# Revit family: Neri_Light Hydra_PUHYDL-Dppp
name_source: partatom
category: Apparecchi per illuminazione
revit_build: Autodesk Revit LT 2018 (Build: 20170223_1515(x64)
units: mm (PartAtom-declared; Revit-internal decimal feet)

## family parameters
Basato su piano di lavoro = No
Condiviso = No
Numero OmniClass = 23.35.47.11
Punto di calcolo locali = No
Quota connettore circolare = Usa diametro
Sempre verticale = Sì
Sorgente d'illuminazione = Sì
Taglio con vuoti quando caricato = No
Tipo di parte = Normale

## types (1)
- PNHYDL_NLG04
    Angolo inclinazione = 90.00°
    CRI = >70
    Class IES = Semi Cut-Off
    Connection = Upright installation on head post or bracket - Hole diam.1,10" for attachment to the support
    Control = COD 02= 1-10V + NCL
    Data Sheet = https://www.nerinorthamerica.com
    Design Country = Italy
    EPA = 0.834 ft²
    Estimated Life = 80.000 h (L85 - Ta 25°C)
    Fasteners = Stainless Steel
    File diagramma fotometrico = PUHYDL_NLG04.IES
    Filtro dei colori = 16777215
    Frequency = 50-60 Hz
    Height = 1' - 11 3/4"
    Height of Installation = From 13.0' to 16.5'
    IK = 06
    IP = 43
    Immagine tipo = <Nessuno>
    LOR = 90 %
    Lampada = LED
    Lenght = 1' - 4 1/2"
    Lighting Distribution/Class = Asymmetric - Mixed Areas
    Luminaire Classification Sysytem = BUG: B1 U3 G1
    Luminous Efficacy = 79 Lm/W
    Manufacturer Country = Italy
    Manufacturer Name = Neri SpA
    MasterFormat 2016 Code = 26 56 00
    MasterFormat 2016 Description = Exterior Lighting
    Material Main = Cast Aluminum
    Modello = PUHYDL-D
    NBS_UniClass2015 Code = Ss_70_80_25_70
    NBS_UniClass2015 Description = Roadway Lighting Systems
    OmniClass Code = 23-35 47 11
    OmniClass Description = Lighting Fixtures
    Operative Temperature = -22°F / +104°F
    Optics = NLG04
    Overvoltage Protection = 4kV/4kV (differential / common mode)
    Painting = Standard color: Exterior Frame_matt black (RAL 9005) - Inside Frame_White (RAL 9010)
    Painting Steps = Information about paint steps used in this product in specific technical sheet
    Product Certification = UL Standard 1598 (C, US)
    Product Name = Light Hydra - LED D
    Produttore = Neri SpA
    Screen = Tempered transparent flat glass
    URL = https://www.nerinorthamerica.com
    UniFormat II Code = D5020
    UniFormat II Description = Lighting and Branch Wiring
    Variazione temperatura colore lampada con luminosità attenuata = <Nessuno>
    Voltage = 120-277 V
    W = 38
    Weight = 44.09 lb
    Width = 2'
